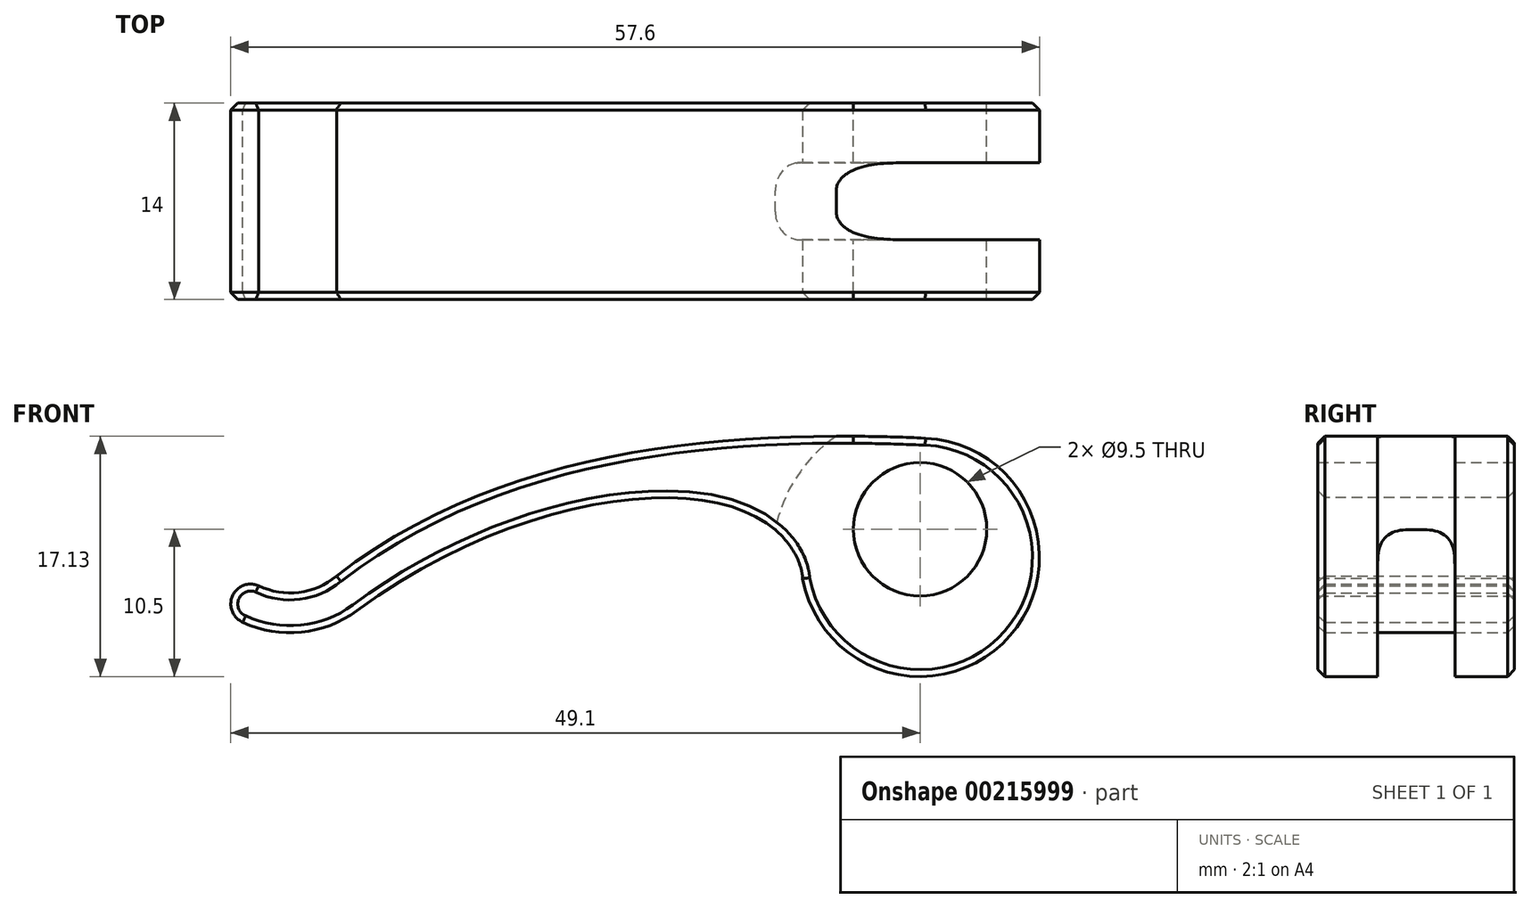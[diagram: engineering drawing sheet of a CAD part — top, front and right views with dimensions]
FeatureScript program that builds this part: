
annotation { "Feature Type Name" : "Feature", "Feature Type Description" : "" }
export const myFeature = defineFeature(function(context is Context, id is Id, definition is map)
    precondition{}
    {
        {
            var Q0;
            Q0=qCreatedBy(makeId("Front.planeOp"),FACE);
            var sketch = newSketch(context, id + "F0", { "sketchPlane" : qUnion([Q0])});
            skPoint(sketch, "E0.visualSharp", {"position": v(59.24, -35.72) * mm});
            skCircle(sketch, "E1", {"center": v(0, -2) * mm, "radius": 8.5 * mm});
            skCircle(sketch, "E2", {"center": v(0, 0) * mm, "radius": 4.5 * mm});
            skFitSpline(sketch, "E3", {"points": [v(0.38, 6.5) * mm, v(-41.57, -3.33) * mm], "startDerivative": vector(-41.9, 1.88) * mm, "endDerivative": vector(-36.18, -27.98) * mm});
            skFitSpline(sketch, "E4", {"points": [v(-8.36, -3.52) * mm, v(-13, 1.47) * mm, v(-40.13, -5.8) * mm], "startDerivative": vector(-1.19, 16.91) * mm, "endDerivative": vector(-43.5, -32.3) * mm});
            skArc(sketch, "E5", {"start": v(-47.12, -4.02) * mm, "mid": v(-44.24, -4.5) * mm, "end": v(-41.57, -3.33) * mm});
            skArc(sketch, "E6.0", {"start": v(-48.24, -6.63) * mm, "mid": v(-44.07, -7.34) * mm, "end": v(-40.13, -5.8) * mm});
            skLineSegment(sketch, "E7", {"start": v(-48.24, -6.63) * mm, "end": v(-47.12, -4.02) * mm});
            skArc(sketch, "E8", {"start": v(-48.24, -6.63) * mm, "mid": v(-48.96, -4.72) * mm, "end": v(-47.03, -4.07) * mm});
            skCircle(sketch, "E9", {"center": v(0, 0) * mm, "radius": 4.75 * mm});
            skLineSegment(sketch, "E10", {"start": v(-4.75, 0) * mm, "end": v(-4.75, 6.63) * mm});
            skLineSegment(sketch, "E11", {"start": v(0, -4.75) * mm, "end": v(8.04, -4.75) * mm});
            skLineSegment(sketch, "E12", {"start": v(-4.75, 0) * mm, "end": v(-4.75, -9.05) * mm});
            skCircle(sketch, "E13", {"center": v(0, -2) * mm, "radius": 10.5 * mm});
            skSolve(sketch);
        }
        {
            var Q0;
            {var subQ4=sQuery(id+"F0.wireOp",EDGE,"E6.0");Q0=makeQuery(id+"F0.imprint","IMPRINT",FACE,{"disambiguationData":[TD([[makeQuery(id+"F0.imprint","IMPRINT",EDGE,{"derivedFrom":subQ4}),1.0]])]});}
            var Q1;
            {var subQ8=sQuery(id+"F0.wireOp",EDGE,"E11");Q1=makeQuery(id+"F0.imprint","IMPRINT",FACE,{"disambiguationData":[TD([[makeQuery(id+"F0.imprint","IMPRINT",EDGE,{"derivedFrom":subQ8}),-1.0]])]});}
            var Q2;
            {var subQ2=sQuery(id+"F0.wireOp",EDGE,"E11");Q2=makeQuery(id+"F0.imprint","IMPRINT",FACE,{"disambiguationData":[TD([[makeQuery(id+"F0.imprint","IMPRINT",EDGE,{"derivedFrom":subQ2}),1.0]])]});}
            var Q3;
            {var subQ0=sQuery(id+"F0.wireOp",EDGE,"E7");Q3=makeQuery(id+"F0.imprint","IMPRINT",FACE,{"disambiguationData":[TD([[makeQuery(id+"F0.imprint","IMPRINT",EDGE,{"derivedFrom":subQ0}),1.0]])]});}
            var Q4;
            {var subQ0=sQuery(id+"F0.wireOp",EDGE,"E3");var subQ1=sQuery(id+"F0.wireOp",EDGE,"E1");var subQ2=makeQuery(id+"F0.imprint","INTERSECT",VERTEX,{"derivedFrom":[subQ1,subQ0]});Q4=makeQuery(id+"F0.imprint","IMPRINT",FACE,{"disambiguationData":[TD([[makeQuery(id+"F0.imprint","IMPRINT",EDGE,{"disambiguationData":[TD([[subQ2,-1.0]])],"derivedFrom":subQ1}),-1.0]])]});}
            var Q5;
            {var subQ0=sQuery(id+"F0.wireOp",EDGE,"E12");Q5=makeQuery(id+"F0.imprint","IMPRINT",FACE,{"disambiguationData":[TD([[makeQuery(id+"F0.imprint","IMPRINT",EDGE,{"derivedFrom":subQ0}),-1.0]])]});}
            var Q6;
            {var subQ0=sQuery(id+"F0.wireOp",EDGE,"E10");var subQ3=sQuery(id+"F0.wireOp",EDGE,"E1");var subQ4=makeQuery(id+"F0.imprint","INTERSECT",VERTEX,{"derivedFrom":[subQ3,subQ0]});Q6=makeQuery(id+"F0.imprint","IMPRINT",FACE,{"disambiguationData":[TD([[makeQuery(id+"F0.imprint","IMPRINT",EDGE,{"disambiguationData":[TD([[subQ4,-1.0]])],"derivedFrom":subQ3}),-1.0]])]});}
            extrude(context, id + "F1", {"entities" : qUnion([Q0, Q1, Q2, Q3, Q4, Q5, Q6]), "endBound" : BoundingType.SYMMETRIC, "depth" : 14 * mm});
        }
        {
            var Q0;
            {var subQ0=sQuery(id+"F0.wireOp",EDGE,"E10");var subQ3=sQuery(id+"F0.wireOp",EDGE,"E1");var subQ4=makeQuery(id+"F0.imprint","INTERSECT",VERTEX,{"derivedFrom":[subQ3,subQ0]});Q0=makeQuery(id+"F0.imprint","IMPRINT",FACE,{"disambiguationData":[TD([[makeQuery(id+"F0.imprint","IMPRINT",EDGE,{"disambiguationData":[TD([[subQ4,-1.0]])],"derivedFrom":subQ3}),-1.0]])]});}
            var Q1;
            {var subQ5=sQuery(id+"F0.wireOp",EDGE,"E11");Q1=makeQuery(id+"F0.imprint","IMPRINT",FACE,{"disambiguationData":[TD([[makeQuery(id+"F0.imprint","IMPRINT",EDGE,{"derivedFrom":subQ5}),1.0]])]});}
            var Q2;
            {var subQ0=sQuery(id+"F0.wireOp",EDGE,"E3");var subQ1=sQuery(id+"F0.wireOp",EDGE,"E1");var subQ2=makeQuery(id+"F0.imprint","INTERSECT",VERTEX,{"derivedFrom":[subQ1,subQ0]});Q2=makeQuery(id+"F0.imprint","IMPRINT",FACE,{"disambiguationData":[TD([[makeQuery(id+"F0.imprint","IMPRINT",EDGE,{"disambiguationData":[TD([[subQ2,-1.0]])],"derivedFrom":subQ1}),-1.0]])]});}
            var Q3;
            {var subQ0=sQuery(id+"F0.wireOp",EDGE,"E12");Q3=makeQuery(id+"F0.imprint","IMPRINT",FACE,{"disambiguationData":[TD([[makeQuery(id+"F0.imprint","IMPRINT",EDGE,{"derivedFrom":subQ0}),-1.0]])]});}
            var Q4;
            {var subQ1=sQuery(id+"F0.wireOp",EDGE,"E1");var subQ5=sQuery(id+"F0.wireOp",EDGE,"E4");var subQ6=makeQuery(id+"F0.imprint","INTERSECT",VERTEX,{"disambiguationData":[OD(0.0)],"derivedFrom":[subQ1,subQ5]});Q4=makeQuery(id+"F0.imprint","IMPRINT",FACE,{"disambiguationData":[TD([[makeQuery(id+"F0.imprint","IMPRINT",EDGE,{"disambiguationData":[TD([[subQ6,1.0]])],"derivedFrom":subQ1}),-1.0]])]});}
            var Q5;
            {var subQ0=sQuery(id+"F0.wireOp",EDGE,"E11");Q5=makeQuery(id+"F0.imprint","IMPRINT",FACE,{"disambiguationData":[TD([[makeQuery(id+"F0.imprint","IMPRINT",EDGE,{"derivedFrom":subQ0}),-1.0]])]});}
            extrude(context, id + "F2", {"entities" : qUnion([Q0, Q1, Q2, Q3, Q4, Q5]), "operationType" : NewBodyOperationType.REMOVE, "endBound" : BoundingType.SYMMETRIC, "depth" : 5.5 * mm});
        }
        {
            var Q0;
            Q0=makeQuery(id+"F2.boolean.opBoolean","COPY",EDGE,{"derivedFrom":makeQuery(id+"F2.opExtrude","CAP_EDGE",EDGE,{"disambiguationData":[OSD([sQuery(id+"F0.wireOp",EDGE,"E13")])],"isStart":true})});
            var Q1;
            Q1=makeQuery(id+"F2.boolean.opBoolean","COPY",EDGE,{"derivedFrom":makeQuery(id+"F2.opExtrude","CAP_EDGE",EDGE,{"disambiguationData":[OSD([sQuery(id+"F0.wireOp",EDGE,"E13")])],"isStart":false})});
            fillet(context, id + "F3", {"entities" : qUnion([Q0, Q1]), "radius" : 2 * mm, "tangentPropagation" : true, "allowEdgeOverflow" : false});
        }
        {
            var Q0;
            Q0=makeQuery(id+"F1.opExtrude","CAP_EDGE",EDGE,{"disambiguationData":[OSD([sQuery(id+"F0.wireOp",EDGE,"E4")])],"isStart":true});
            var Q1;
            Q1=makeQuery(id+"F1.opExtrude","CAP_EDGE",EDGE,{"disambiguationData":[OSD([sQuery(id+"F0.wireOp",EDGE,"E1")])],"isStart":true});
            var Q2;
            Q2=makeQuery(id+"F1.opExtrude","CAP_EDGE",EDGE,{"disambiguationData":[OSD([sQuery(id+"F0.wireOp",EDGE,"E3")])],"isStart":true});
            var Q3;
            Q3=makeQuery(id+"F1.opExtrude","CAP_EDGE",EDGE,{"disambiguationData":[OSD([sQuery(id+"F0.wireOp",EDGE,"E6.0")])],"isStart":true});
            var Q4;
            Q4=makeQuery(id+"F1.opExtrude","CAP_EDGE",EDGE,{"disambiguationData":[OSD([sQuery(id+"F0.wireOp",EDGE,"E5")])],"isStart":true});
            var Q5;
            Q5=makeQuery(id+"F1.opExtrude","CAP_EDGE",EDGE,{"disambiguationData":[OSD([sQuery(id+"F0.wireOp",EDGE,"E8")])],"isStart":true});
            var Q6;
            Q6=makeQuery(id+"F1.opExtrude","CAP_EDGE",EDGE,{"disambiguationData":[OSD([sQuery(id+"F0.wireOp",EDGE,"E6.0")])],"isStart":false});
            var Q7;
            Q7=makeQuery(id+"F1.opExtrude","CAP_EDGE",EDGE,{"disambiguationData":[OSD([sQuery(id+"F0.wireOp",EDGE,"E8")])],"isStart":false});
            var Q8;
            Q8=makeQuery(id+"F1.opExtrude","CAP_EDGE",EDGE,{"disambiguationData":[OSD([sQuery(id+"F0.wireOp",EDGE,"E5")])],"isStart":false});
            var Q9;
            Q9=makeQuery(id+"F1.opExtrude","CAP_EDGE",EDGE,{"disambiguationData":[OSD([sQuery(id+"F0.wireOp",EDGE,"E3")])],"isStart":false});
            var Q10;
            Q10=makeQuery(id+"F1.opExtrude","CAP_EDGE",EDGE,{"disambiguationData":[OSD([sQuery(id+"F0.wireOp",EDGE,"E4")])],"isStart":false});
            var Q11;
            Q11=makeQuery(id+"F1.opExtrude","CAP_EDGE",EDGE,{"disambiguationData":[OSD([sQuery(id+"F0.wireOp",EDGE,"E1")])],"isStart":false});
            chamfer(context, id + "F4", {"entities" : qUnion([Q0, Q1, Q2, Q3, Q4, Q5, Q6, Q7, Q8, Q9, Q10, Q11]), "width" : .5 * mm, "tangentPropagation" : true});
        }
    });
